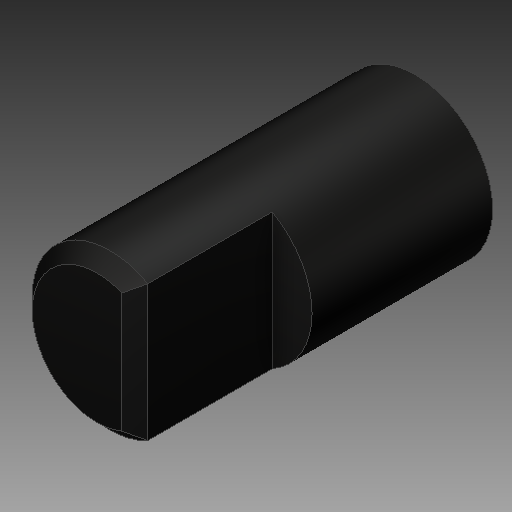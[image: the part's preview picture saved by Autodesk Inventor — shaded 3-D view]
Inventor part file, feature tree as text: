
AUTODESK INVENTOR PART (.ipt)
format: ipt  version: 2018 (Build 220112000, 112)  size: 117,248 bytes
history: native  units: mm
features: extrude x2, sketch x2, chamfer x1
ambient origin geometry x8: Origin, YZ Plane, XZ Plane, XY Plane, X Axis, Y Axis, Z Axis, Center Point
bodies: Solid1 (feature_tree)
feature tree (5):
  extrude  "Extrusion1"  Depth=12.27mm TaperAngle=0.0deg
  extrude  "Extrusion2"  Depth=5.3mm TaperAngle=0.0deg
  chamfer  "Chamfer1"  Distance=0.5mm Angle=45.0deg
  sketch  "Sketch1"  dims[d0=6.0mm d1=12.27mm d2=0.0mm]
  sketch  "Sketch2"  dims[d3=4.46mm d4=5.3mm d5=0.0mm d6=0.5mm d7=2.0mm d8=45.0deg]
